# Revit family: Lighting_Outdoor-WallMnt
name_source: partatom
category: Lighting Fixtures
units: mm (PartAtom-declared; Revit-internal decimal feet)

## family parameters
Always vertical = Yes
Classification Number = 23.80.70.14
Cut with Voids When Loaded = No
Light Source = Yes
Maintain Annotation Orientation = No
Part Type = Normal
Room Calculation Point = No
Round Connector Dimension = Use Diameter
Shared = No
Work Plane-Based = No

## types (4) — shared parameters
Color Filter = 16777215
Construction Details = http://www.arcat.com
Default Elevation = 0' - 0"
Dimming Lamp Color Temperature Shift = <None>
Expected Lifespan (Years) = 20
Green Building-LEED = http://www.arcat.com
Keynote = 16520
Light Source Symbol Size = 2' - 0"
Maintenance Schedule (Months) = 12
Manufacturer = Generic
Manufacturer Fax = (203) 929-2444
Manufacturer Website = http://www.arcat.com
Model = Generic
Pole Diameter = 0' - 8"
Pole Wall Thickness = 0' - 0 1/2"
Poles = 1
Power Factor = 1
Product Data = http://www.arcat.com
Product Properties = http://www.arcat.com
Shroud Material = ARCAT - Metal - Steel - Painted - Brown
Specification = http://www.arcat.com
Voltage = 120 V
Warranty Duration (Years) = 1
armrad = 0' - 2"
brktthk = 0' - 1 29/32"
id = 0' - 3 1/2"
shrwl = 0' - 0 1/4"

## per-type parameters (varying)
| type | Amperage | Apparent Power | Arm Declination | Arm Reach | Assembly Code | Description | Diffuser | Lamp | Lamps | Total Amperage | Total Lumens | Total Wattage | Watts_Bulb |
| 400W MH Bulb | 0.909091 | 0 VA | 3' - 0" | 6' - 0" | D5020280 | 400W Metal Halide Area Light | ARCAT - Plastic - Polycarbonate_Translucent-Clear | Metal Halide | 4 | 3.636364 | 144000 | 1600 | 400 |
| 400W HPS Bulb | 0.909091 | 0 VA | 3' - 0" | 6' - 0" | D5020220 | 400 Watt Hight Pressure Sodium Area Light | ARCAT - Plastic - Polycarbonate_Translucent-Yellow | High Pressure Sodium | 4 | 3.636364 | 200000 | 1600 | 400 |
| 1000W HPS Bulb | 2.272727 | 600 VA | 1' - 6" | 3' - 0" | D5020280 | 1000 Watt Hight Pressure Sodium Area Light | ARCAT - Plastic - Polycarbonate_Translucent-Yellow | High Pressure Sodium | 1 | 2.272727 | 125000 | 1000 | 1000 |
| 1000W MH Bulb | 2.272727 | 0 VA | 3' - 0" | 6' - 0" | D5020280 | 1000W Metal Halide Area Light | ARCAT - Plastic - Polycarbonate_Translucent-Clear | Metal Halide | 4 | 9.090909 | 360000 | 4000 | 1000 |

## geometry (parser evidence)
native form markers: Sweep x11
no freeform markers — native parametric forms only
